# Revit family: AssaAbloy_VersaMax2.0FGI_Sliding ICU
name_source: partatom
category: Doors
units: mm (PartAtom-declared; Revit-internal decimal feet)

## family parameters
Always vertical = Yes
Cut with Voids When Loaded = No
Host = Wall
OmniClass Number = 23.30.10.00
OmniClass Title = Doors
Room Calculation Point = No
Shared = No

## types (2) — shared parameters
Active Leaf Height = 6' - 11"
CL of Muntin from Floor = 3' - 5 1/2"
Description = The VersaMax 2.0 FGI redefines ICU door performance by delivering the widest clear door opening (CDO) available in the market for an 8-foot overall frame width (OFW).
Engineered to meet the stringent 2022 FGI guidelines adopted by over 40 states, including California’s CBC requirements, the VersaMax 2.0 FGI ensures compliance without compromise.
This innovative design enables healthcare facilities to meet code while enhancing patient access and operational efficiency. With newly developed components and a smart redesign of the VersaMax platform, the VersaMax 2.0 FGI offers unmatched value, performance, and code compliance.
Function = Interior
Glass Thickness = 0' - 0 1/4"
Hardware Height = 3' - 0"
Header Rail Height Control = 0' - 4"
Height = 7' - 6"
Height Control = 7' - 6"
Manufacturer = ASSA ABLOY Entrance Systems
Muntin Height from Floor = 3' - 4 5/8"
Panel Thickness = 0' - 1 3/4"
Rough Height = 7' - 6 1/2"
Rough Height Offset = 0' - 0 1/2"
Rough Width Offset = 0' - 0 1/4"
Sidelite Header Height = 0' - 4"
Sidelite Height = 7' - 0 1/2"
URL = https://www.assaabloyentrance.us
Wall Closure = By host

## per-type parameters (varying)
| type | Active Leaf Width Control | Clear Opening Width | Model | Muntin Height | Rough Width | Sidelite Width Control | Width | Width Control |
| 96" W x 90" H | 4' - 1" | 3' - 8 1/2" | VMS2FBO-8 | 0' - 0" | 8' - 0 1/2" | 3' - 9 5/8" | 8' - 0" | 8' - 0" |
| 102" W x 90" H | 4' - 4" | 3' - 11 1/2" | VMS2FBO-8
VMS2FBO-8
VMS2FBO-8
VMS2FBO-8
VMS2FBO-8-6
VMS2FBO-8 | 0' - 1 3/4" | 8' - 6 1/2" | 4' - 0 5/8" | 8' - 6" | 8' - 6" |

## geometry (parser evidence)
native form markers: Sweep x17
no freeform markers — native parametric forms only
